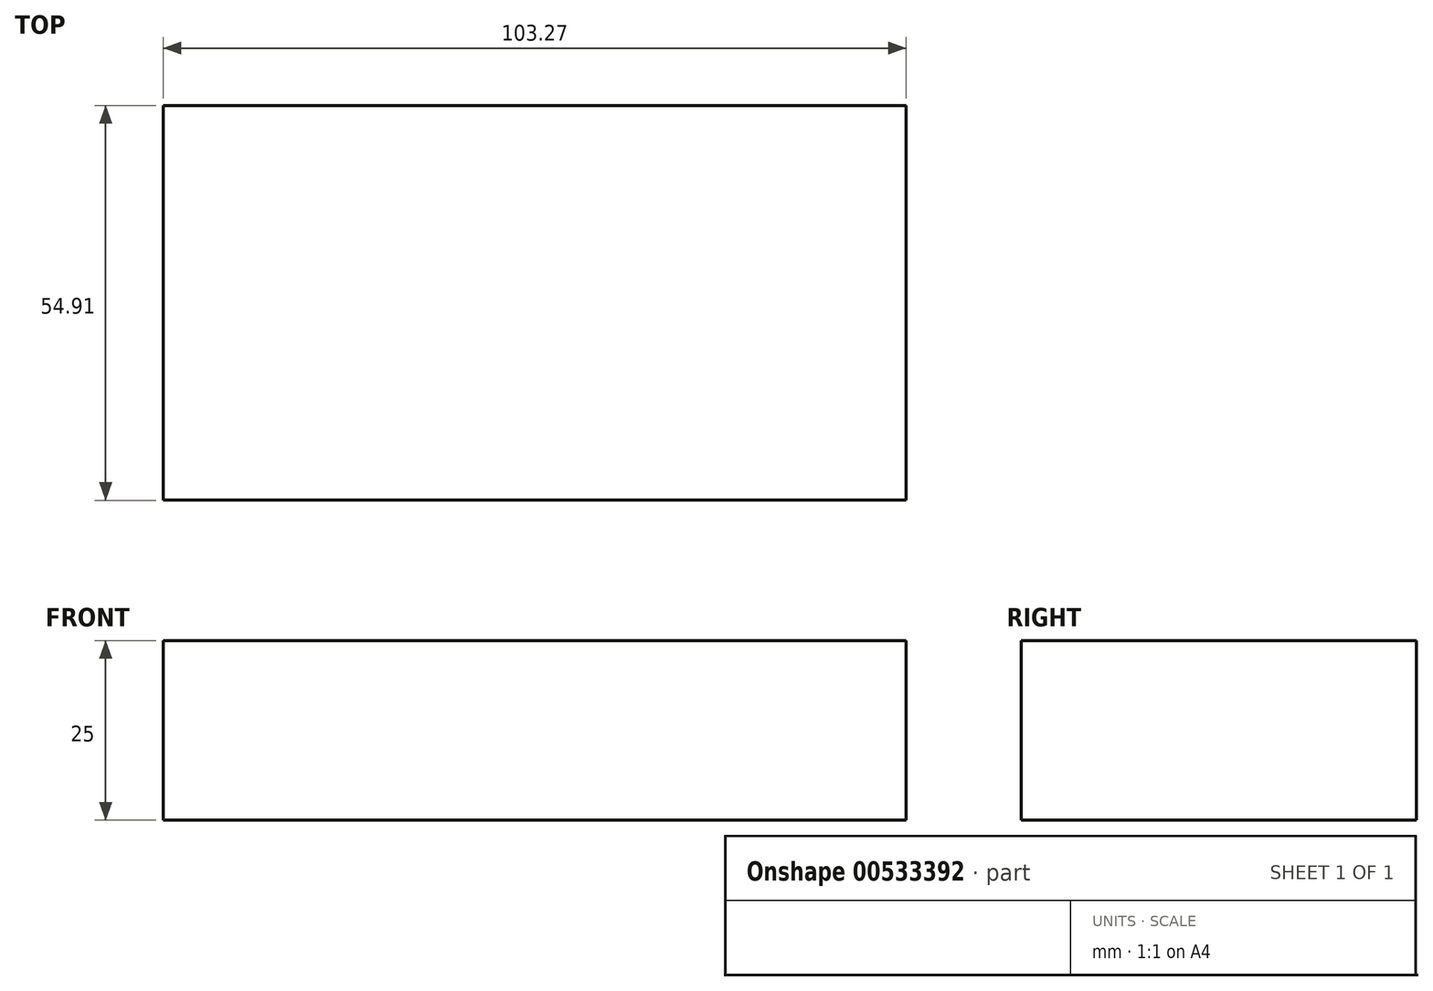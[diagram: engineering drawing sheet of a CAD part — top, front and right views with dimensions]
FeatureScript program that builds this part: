
annotation { "Feature Type Name" : "Feature", "Feature Type Description" : "" }
export const myFeature = defineFeature(function(context is Context, id is Id, definition is map)
    precondition{}
    {
        {
            var Q0;
            Q0=qCreatedBy(makeId("Top.planeOp"),FACE);
            var sketch = newSketch(context, id + "F0", { "sketchPlane" : qUnion([Q0])});
            skLineSegment(sketch, "E0.bottom", {"start": v(-51.07, 31.52) * mm, "end": v(52.2, 31.52) * mm});
            skLineSegment(sketch, "E0.top", {"start": v(-51.07, -23.39) * mm, "end": v(52.2, -23.39) * mm});
            skLineSegment(sketch, "E0.left", {"start": v(-51.07, 31.52) * mm, "end": v(-51.07, -23.39) * mm});
            skLineSegment(sketch, "E0.right", {"start": v(52.2, 31.52) * mm, "end": v(52.2, -23.39) * mm});
            skSolve(sketch);
        }
        {
            var Q0;
            Q0 = qSketchRegion(id + "F0", true);
            extrude(context, id + "F1", {"entities" : qUnion([Q0]), "oppositeDirection" : true, "depth" : 25 * mm, "offsetDistance" : 25 * mm});
        }
    });
